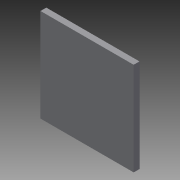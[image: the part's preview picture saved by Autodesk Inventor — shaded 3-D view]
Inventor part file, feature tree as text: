
AUTODESK INVENTOR PART (.ipt)
format: ipt  version: 2013 (Build 170138000, 138)  size: 76,800 bytes
history: native  units: in
note: dims shown in document units (in); Inventor stores cm internally (conversion verified against a paired STEP export)
features: sketch x2, extrude x1
ambient origin geometry x8: Origin, YZ Plane, XZ Plane, XY Plane, X Axis, Y Axis, Z Axis, Center Point
bodies: Solid1 (feature_tree)
feature tree (3):
  extrude  "Extrusion1"  Depth=0.9449in
  sketch  "Sketch2"  dims[d4=0.9449in]
  sketch  "Sketch1"  dims[d0=0.0591in d1=0.0in d2=0.9449in]
